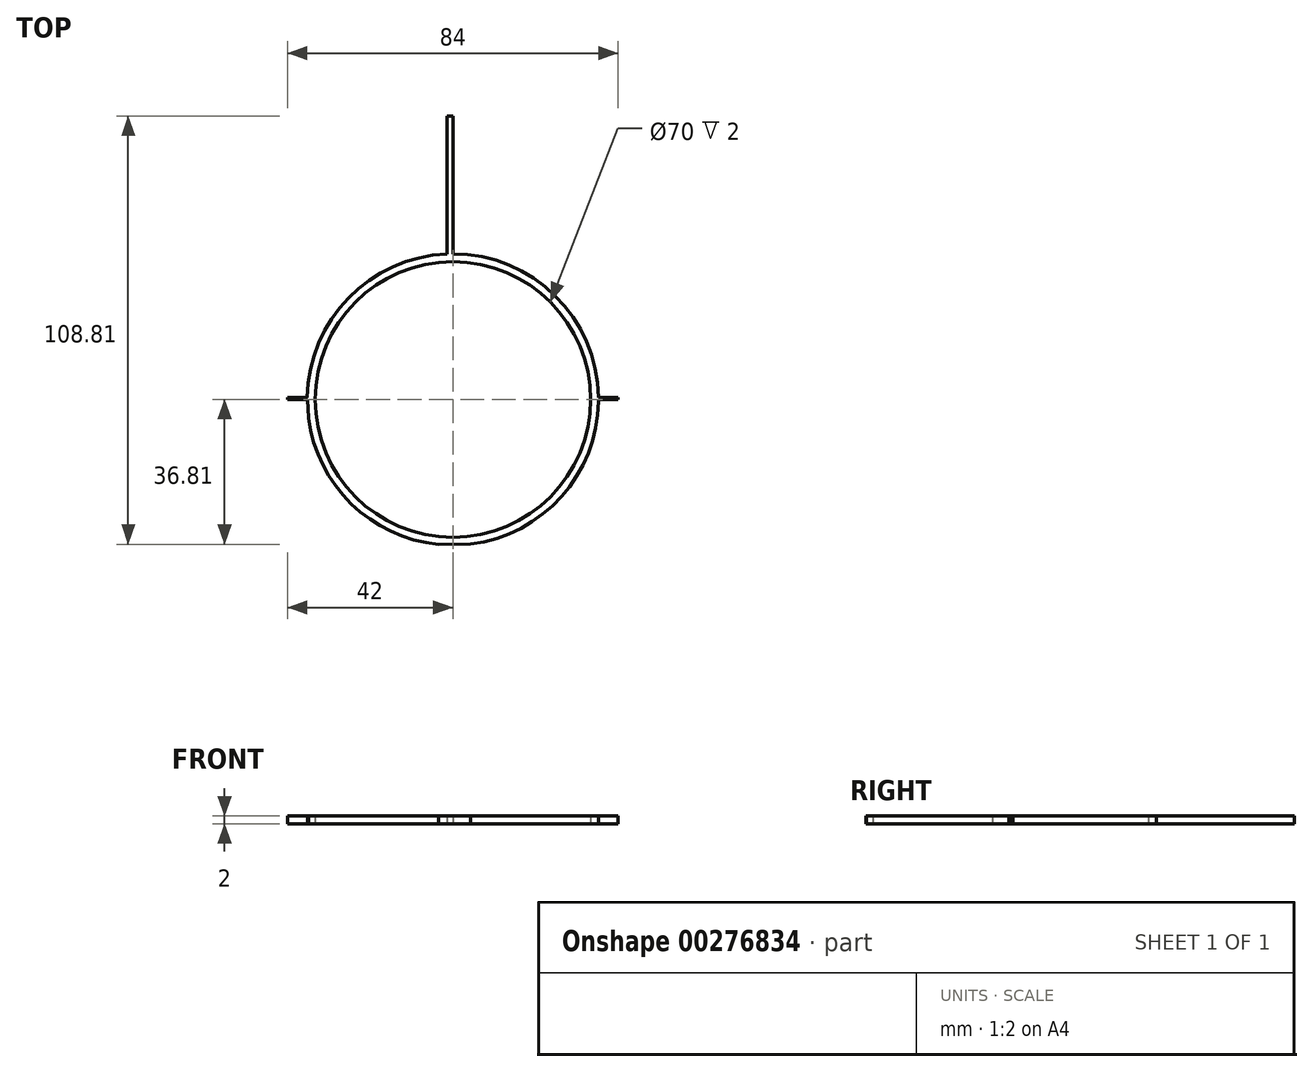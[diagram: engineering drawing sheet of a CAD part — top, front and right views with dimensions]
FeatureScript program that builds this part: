
annotation { "Feature Type Name" : "Feature", "Feature Type Description" : "" }
export const myFeature = defineFeature(function(context is Context, id is Id, definition is map)
    precondition{}
    {
        {
            var Q0;
            Q0=qCreatedBy(makeId("Top.planeOp"),FACE);
            var sketch = newSketch(context, id + "F0", { "sketchPlane" : qUnion([Q0])});
            skCircle(sketch, "E0", {"center": v(0, 0) * mm, "radius": 35 * mm});
            skArc(sketch, "E1", {"start": v(-1.5, 36.97) * mm, "mid": v(-26.51, 25.8) * mm, "end": v(-37, 0.5) * mm});
            skArc(sketch, "E2", {"start": v(37, 0.5) * mm, "mid": v(25.99, 26.34) * mm, "end": v(0, 37) * mm});
            skArc(sketch, "E3", {"start": v(4.5, -36.73) * mm, "mid": v(27.54, -24.71) * mm, "end": v(37, -0.5) * mm});
            skArc(sketch, "E4", {"start": v(-36.7, -4.68) * mm, "mid": v(-25.81, -26.5) * mm, "end": v(-3.7, -36.81) * mm});
            skLineSegment(sketch, "E5", {"start": v(-36.97, 0) * mm, "end": v(-36.7, -4.68) * mm});
            skLineSegment(sketch, "E6", {"start": v(37, 0) * mm, "end": v(37, -0.5) * mm});
            skLineSegment(sketch, "E7", {"start": v(4.5, -36.73) * mm, "end": v(-3.7, -36.81) * mm});
            skPoint(sketch, "E8.start.orphan", {"position": v(37, 0) * mm});
            skPoint(sketch, "E9.start.orphan", {"position": v(0, -36.77) * mm});
            skPoint(sketch, "E10.start.orphan", {"position": v(0, 35) * mm});
            skPoint(sketch, "E11.start.orphan", {"position": v(-35, 0) * mm});
            skLineSegment(sketch, "E12.bottom", {"start": v(-37, 0.5) * mm, "end": v(-42, 0.5) * mm});
            skLineSegment(sketch, "E12.top", {"start": v(-36.87, 0) * mm, "end": v(-41.99, 0) * mm});
            skLineSegment(sketch, "E12.right", {"start": v(-42, 0.5) * mm, "end": v(-41.99, 0) * mm});
            skLineSegment(sketch, "E13", {"start": v(-1.5, 36.97) * mm, "end": v(-1.5, 72) * mm});
            skLineSegment(sketch, "E14", {"start": v(-1.5, 72) * mm, "end": v(0, 72) * mm});
            skLineSegment(sketch, "E15", {"start": v(0, 72) * mm, "end": v(0, 37) * mm});
            skLineSegment(sketch, "E16", {"start": v(37, 0.5) * mm, "end": v(42, 0.5) * mm});
            skLineSegment(sketch, "E17", {"start": v(42, 0.5) * mm, "end": v(42, 0) * mm});
            skLineSegment(sketch, "E18", {"start": v(42, 0) * mm, "end": v(37, 0) * mm});
            skSolve(sketch);
        }
        {
            var Q0;
            Q0=makeQuery(id+"F0.imprint","IMPRINT",FACE,{"disambiguationData":[TD([[makeQuery(id+"F0.imprint","IMPRINT",EDGE,{"derivedFrom":sQuery(id+"F0.wireOp",EDGE,"E0")}),-1.0]])]});
            extrude(context, id + "F1", {"entities" : qUnion([Q0]), "endBound" : BoundingType.SYMMETRIC, "depth" : 2 * mm});
        }
    });
